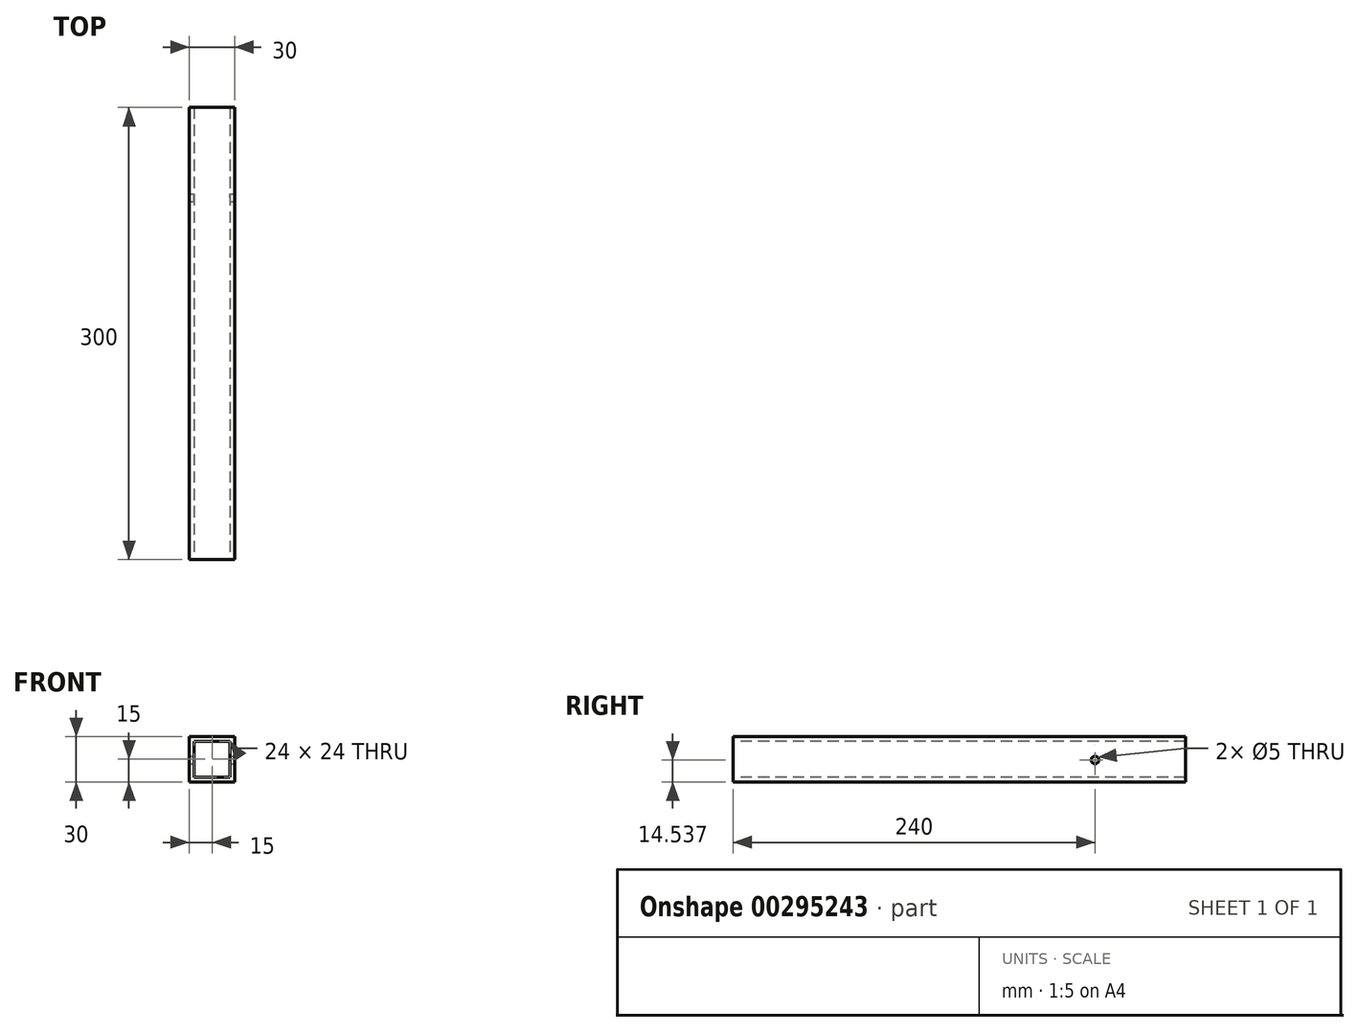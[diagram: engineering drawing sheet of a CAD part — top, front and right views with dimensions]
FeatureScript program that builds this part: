
annotation { "Feature Type Name" : "Feature", "Feature Type Description" : "" }
export const myFeature = defineFeature(function(context is Context, id is Id, definition is map)
    precondition{}
    {
        {
            var Q0;
            Q0=qCreatedBy(makeId("Front.planeOp"),FACE);
            var sketch = newSketch(context, id + "F0", { "sketchPlane" : qUnion([Q0])});
            skLineSegment(sketch, "E0.bottom", {"start": v(0, 0) * mm, "end": v(30, 0) * mm});
            skLineSegment(sketch, "E0.top", {"start": v(0, 30) * mm, "end": v(30, 30) * mm});
            skLineSegment(sketch, "E0.left", {"start": v(0, 0) * mm, "end": v(0, 30) * mm});
            skLineSegment(sketch, "E0.right", {"start": v(30, 0) * mm, "end": v(30, 30) * mm});
            skSolve(sketch);
        }
        {
            var Q0;
            Q0=makeQuery(id+"F0.imprint","IMPRINT",FACE,{"disambiguationData":[TD([[makeQuery(id+"F0.imprint","IMPRINT",EDGE,{"derivedFrom":sQuery(id+"F0.wireOp",EDGE,"E0.bottom")}),1.0]])]});
            extrude(context, id + "F1", {"entities" : qUnion([Q0]), "depth" : 300 * mm});
        }
        {
            var Q0;
            Q0=makeQuery(id+"F1.opExtrude","CAP_FACE",FACE,{"disambiguationData":[OSD([sQuery(id+"F0.wireOp",EDGE,"E0.bottom"),sQuery(id+"F0.wireOp",EDGE,"E0.top"),sQuery(id+"F0.wireOp",EDGE,"E0.left"),sQuery(id+"F0.wireOp",EDGE,"E0.right")])],"isStart":false});
            var sketch = newSketch(context, id + "F2", { "sketchPlane" : qUnion([Q0])});
            skLineSegment(sketch, "E1.bottom", {"start": v(27, 27) * mm, "end": v(3, 27) * mm});
            skLineSegment(sketch, "E1.top", {"start": v(27, 3) * mm, "end": v(3, 3) * mm});
            skLineSegment(sketch, "E1.left", {"start": v(27, 27) * mm, "end": v(27, 3) * mm});
            skLineSegment(sketch, "E1.right", {"start": v(3, 27) * mm, "end": v(3, 3) * mm});
            skSolve(sketch);
        }
        {
            var Q0;
            Q0 = qSketchRegion(id + "F2", true);
            extrude(context, id + "F3", {"entities" : qUnion([Q0]), "operationType" : NewBodyOperationType.REMOVE, "endBound" : BoundingType.THROUGH_ALL, "oppositeDirection" : true, "depth" : 25 * mm});
        }
        {
            var Q0;
            Q0=makeQuery(id+"F1.opExtrude","SWEPT_FACE",FACE,{"disambiguationData":[OSD([sQuery(id+"F0.wireOp",EDGE,"E0.right")])]});
            var sketch = newSketch(context, id + "F4", { "sketchPlane" : qUnion([Q0])});
            skCircle(sketch, "E2", {"center": v(-60, 14.54) * mm, "radius": 2.5 * mm});
            skSolve(sketch);
        }
        {
            var Q0;
            Q0 = qSketchRegion(id + "F4", true);
            extrude(context, id + "F5", {"entities" : qUnion([Q0]), "operationType" : NewBodyOperationType.REMOVE, "endBound" : BoundingType.THROUGH_ALL, "oppositeDirection" : true, "depth" : 25 * mm});
        }
    });
